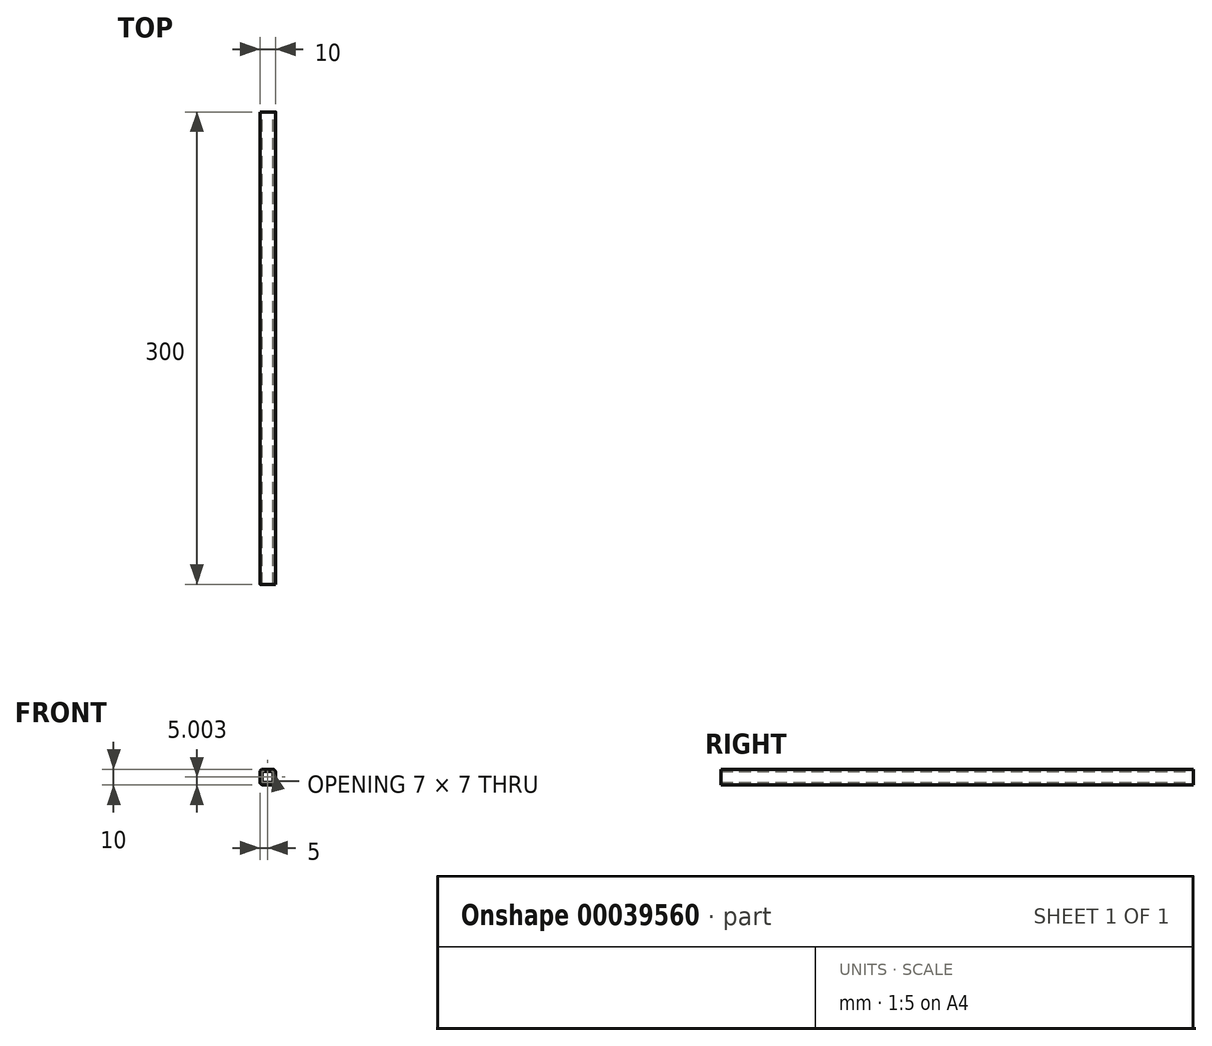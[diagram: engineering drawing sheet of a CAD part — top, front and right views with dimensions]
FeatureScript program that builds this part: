
annotation { "Feature Type Name" : "Feature", "Feature Type Description" : "" }
export const myFeature = defineFeature(function(context is Context, id is Id, definition is map)
    precondition{}
    {
        {
            var Q0;
            Q0=qCreatedBy(makeId("Front.planeOp"),FACE);
            var sketch = newSketch(context, id + "F0", { "sketchPlane" : qUnion([Q0])});
            skLineSegment(sketch, "E0.bottom", {"start": v(60.8, 9.8) * mm, "end": v(70.8, 9.8) * mm});
            skLineSegment(sketch, "E0.top", {"start": v(60.8, 19.8) * mm, "end": v(70.8, 19.8) * mm});
            skLineSegment(sketch, "E0.left", {"start": v(60.8, 9.8) * mm, "end": v(60.8, 19.8) * mm});
            skLineSegment(sketch, "E0.right", {"start": v(70.8, 9.8) * mm, "end": v(70.8, 19.8) * mm});
            skSolve(sketch);
        }
        {
            var Q0;
            Q0=makeQuery(id+"F0.imprint","IMPRINT",FACE,{"disambiguationData":[TD([[makeQuery(id+"F0.imprint","IMPRINT",EDGE,{"derivedFrom":sQuery(id+"F0.wireOp",EDGE,"E0.bottom")}),1.0]])]});
            extrude(context, id + "F1", {"entities" : qUnion([Q0]), "depth" : 300 * mm});
        }
        {
            var Q0;
            Q0=makeQuery(id+"F1.opExtrude","SWEPT_EDGE",EDGE,{"disambiguationData":[OSD([sQuery(id+"F0.wireOp",EDGE,"E0.top"),sQuery(id+"F0.wireOp",EDGE,"E0.right")])]});
            var Q1;
            Q1=makeQuery(id+"F1.opExtrude","SWEPT_EDGE",EDGE,{"disambiguationData":[OSD([sQuery(id+"F0.wireOp",EDGE,"E0.top"),sQuery(id+"F0.wireOp",EDGE,"E0.left")])]});
            var Q2;
            Q2=makeQuery(id+"F1.opExtrude","SWEPT_EDGE",EDGE,{"disambiguationData":[OSD([sQuery(id+"F0.wireOp",EDGE,"E0.bottom"),sQuery(id+"F0.wireOp",EDGE,"E0.right")])]});
            var Q3;
            Q3=makeQuery(id+"F1.opExtrude","SWEPT_EDGE",EDGE,{"disambiguationData":[OSD([sQuery(id+"F0.wireOp",EDGE,"E0.bottom"),sQuery(id+"F0.wireOp",EDGE,"E0.left")])]});
            fillet(context, id + "F2", {"entities" : qUnion([Q0, Q1, Q2, Q3]), "radius" : 2 * mm, "tangentPropagation" : true, "allowEdgeOverflow" : false});
        }
        {
            var Q0;
            Q0=makeQuery(id+"F1.opExtrude","CAP_FACE",FACE,{"disambiguationData":[OSD([sQuery(id+"F0.wireOp",EDGE,"E0.bottom"),sQuery(id+"F0.wireOp",EDGE,"E0.top"),sQuery(id+"F0.wireOp",EDGE,"E0.left"),sQuery(id+"F0.wireOp",EDGE,"E0.right")])],"isStart":false});
            var Q1;
            Q1=makeQuery(id+"F1.opExtrude","CAP_FACE",FACE,{"disambiguationData":[OSD([sQuery(id+"F0.wireOp",EDGE,"E0.bottom"),sQuery(id+"F0.wireOp",EDGE,"E0.top"),sQuery(id+"F0.wireOp",EDGE,"E0.left"),sQuery(id+"F0.wireOp",EDGE,"E0.right")])],"isStart":true});
            shell(context, id + "F3", {"entities" : qUnion([Q0, Q1]), "thickness" : 1.5 * mm});
        }
    });
